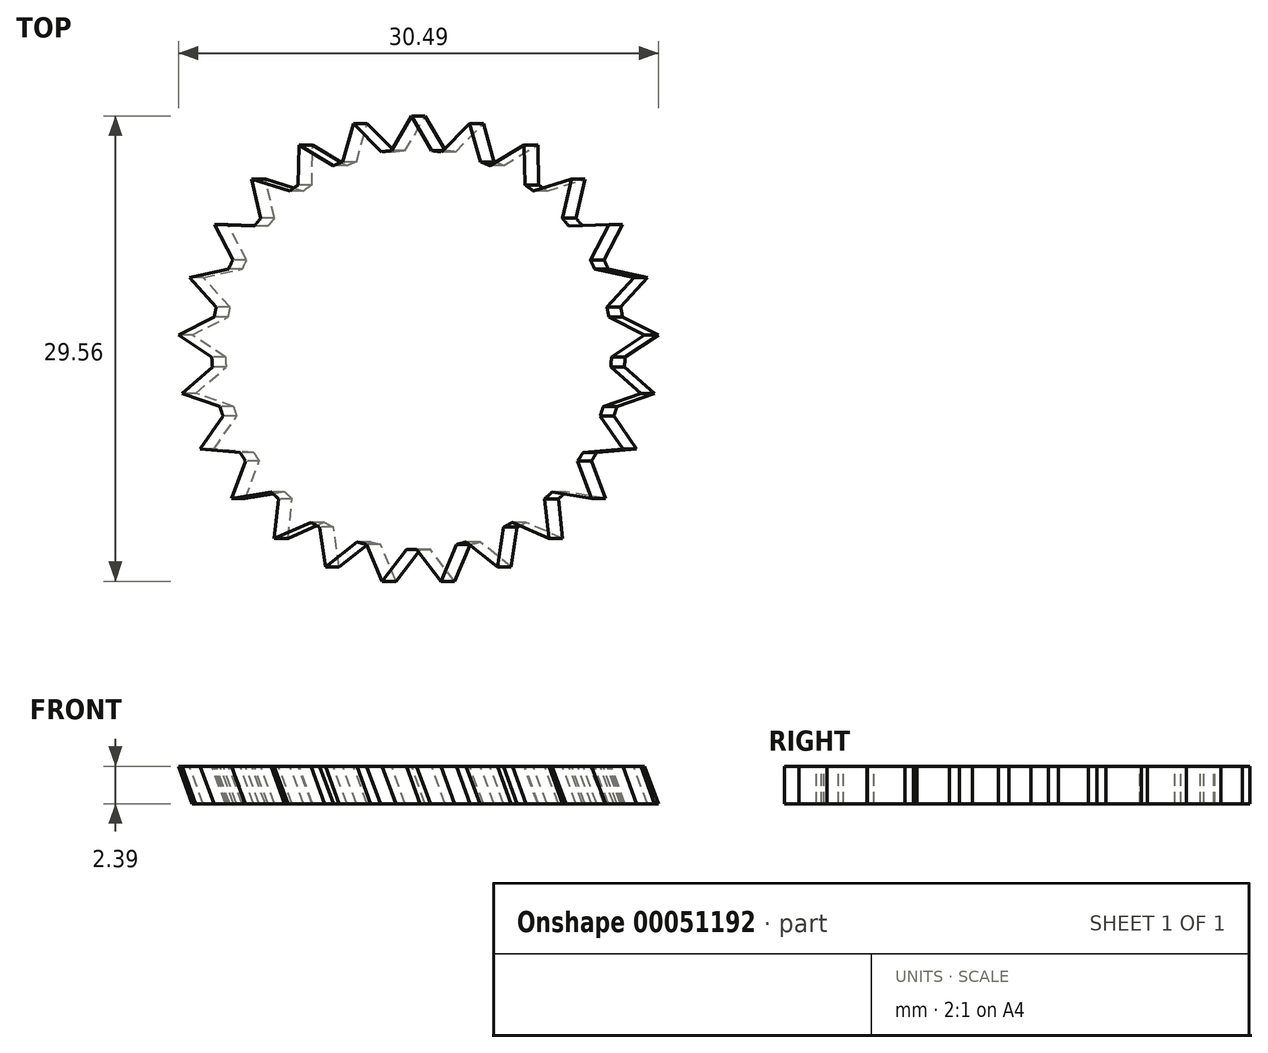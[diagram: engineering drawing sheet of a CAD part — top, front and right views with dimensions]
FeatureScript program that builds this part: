
annotation { "Feature Type Name" : "Feature", "Feature Type Description" : "" }
export const myFeature = defineFeature(function(context is Context, id is Id, definition is map)
    precondition{}
    {
        {
            var Q0;
            Q0=qCreatedBy(makeId("Top.planeOp"),FACE);
            var sketch = newSketch(context, id + "F0", { "sketchPlane" : qUnion([Q0])});
            skArc(sketch, "E0", {"start": v(-1.27, 12.64) * mm, "mid": v(-1.6, 12.6) * mm, "end": v(-1.91, 12.56) * mm});
            skLineSegment(sketch, "E1.1", {"start": v(-1.27, 12.64) * mm, "end": v(0, 14.84) * mm});
            skLineSegment(sketch, "E1.2", {"start": v(0, 14.84) * mm, "end": v(1.27, 12.64) * mm});
            skLineSegment(sketch, "E2.1.0", {"start": v(-4.37, 11.92) * mm, "end": v(-3.69, 14.37) * mm});
            skLineSegment(sketch, "E2.1.1", {"start": v(-3.69, 14.37) * mm, "end": v(-1.91, 12.56) * mm});
            skLineSegment(sketch, "E2.2.0", {"start": v(-7.2, 10.46) * mm, "end": v(-7.15, 13) * mm});
            skLineSegment(sketch, "E2.2.1", {"start": v(-7.15, 13) * mm, "end": v(-4.97, 11.69) * mm});
            skLineSegment(sketch, "E2.3.0", {"start": v(-9.58, 8.34) * mm, "end": v(-10.16, 10.82) * mm});
            skLineSegment(sketch, "E2.3.1", {"start": v(-10.16, 10.82) * mm, "end": v(-7.72, 10.08) * mm});
            skLineSegment(sketch, "E2.4.0", {"start": v(-11.35, 5.7) * mm, "end": v(-12.53, 7.95) * mm});
            skLineSegment(sketch, "E2.4.1", {"start": v(-12.53, 7.95) * mm, "end": v(-9.99, 7.84) * mm});
            skLineSegment(sketch, "E2.5.0", {"start": v(-12.41, 2.7) * mm, "end": v(-14.1, 4.58) * mm});
            skLineSegment(sketch, "E2.5.1", {"start": v(-14.1, 4.58) * mm, "end": v(-11.63, 5.11) * mm});
            skLineSegment(sketch, "E2.6.0", {"start": v(-12.7, -0.47) * mm, "end": v(-14.8, 0.93) * mm});
            skLineSegment(sketch, "E2.6.1", {"start": v(-14.8, 0.93) * mm, "end": v(-12.53, 2.06) * mm});
            skLineSegment(sketch, "E2.7.0", {"start": v(-12.17, -3.62) * mm, "end": v(-14.57, -2.78) * mm});
            skLineSegment(sketch, "E2.7.1", {"start": v(-14.57, -2.78) * mm, "end": v(-12.65, -1.12) * mm});
            skLineSegment(sketch, "E2.8.0", {"start": v(-10.9, -6.53) * mm, "end": v(-13.42, -6.32) * mm});
            skLineSegment(sketch, "E2.8.1", {"start": v(-13.42, -6.32) * mm, "end": v(-11.97, -4.23) * mm});
            skLineSegment(sketch, "E2.9.0", {"start": v(-8.93, -9.03) * mm, "end": v(-11.43, -9.46) * mm});
            skLineSegment(sketch, "E2.9.1", {"start": v(-11.43, -9.46) * mm, "end": v(-10.55, -7.08) * mm});
            skLineSegment(sketch, "E2.10.0", {"start": v(-6.4, -10.97) * mm, "end": v(-8.72, -12) * mm});
            skLineSegment(sketch, "E2.10.1", {"start": v(-8.72, -12) * mm, "end": v(-8.45, -9.48) * mm});
            skLineSegment(sketch, "E2.11.0", {"start": v(-3.47, -12.22) * mm, "end": v(-5.46, -13.8) * mm});
            skLineSegment(sketch, "E2.11.1", {"start": v(-5.46, -13.8) * mm, "end": v(-5.83, -11.28) * mm});
            skLineSegment(sketch, "E2.12.0", {"start": v(-0.32, -12.7) * mm, "end": v(-1.86, -14.72) * mm});
            skLineSegment(sketch, "E2.12.1", {"start": v(-1.86, -14.72) * mm, "end": v(-2.84, -12.38) * mm});
            skLineSegment(sketch, "E2.13.0", {"start": v(2.84, -12.38) * mm, "end": v(1.86, -14.72) * mm});
            skLineSegment(sketch, "E2.13.1", {"start": v(1.86, -14.72) * mm, "end": v(0.32, -12.7) * mm});
            skLineSegment(sketch, "E2.14.0", {"start": v(5.83, -11.28) * mm, "end": v(5.46, -13.8) * mm});
            skLineSegment(sketch, "E2.14.1", {"start": v(5.46, -13.8) * mm, "end": v(3.47, -12.22) * mm});
            skLineSegment(sketch, "E2.15.0", {"start": v(8.45, -9.48) * mm, "end": v(8.72, -12) * mm});
            skLineSegment(sketch, "E2.15.1", {"start": v(8.72, -12) * mm, "end": v(6.4, -10.97) * mm});
            skLineSegment(sketch, "E2.16.0", {"start": v(10.55, -7.08) * mm, "end": v(11.43, -9.46) * mm});
            skLineSegment(sketch, "E2.16.1", {"start": v(11.43, -9.46) * mm, "end": v(8.93, -9.03) * mm});
            skLineSegment(sketch, "E2.17.0", {"start": v(11.97, -4.23) * mm, "end": v(13.42, -6.32) * mm});
            skLineSegment(sketch, "E2.17.1", {"start": v(13.42, -6.32) * mm, "end": v(10.9, -6.53) * mm});
            skLineSegment(sketch, "E2.18.0", {"start": v(12.65, -1.12) * mm, "end": v(14.57, -2.78) * mm});
            skLineSegment(sketch, "E2.18.1", {"start": v(14.57, -2.78) * mm, "end": v(12.17, -3.62) * mm});
            skLineSegment(sketch, "E2.19.0", {"start": v(12.53, 2.06) * mm, "end": v(14.8, 0.93) * mm});
            skLineSegment(sketch, "E2.19.1", {"start": v(14.8, 0.93) * mm, "end": v(12.7, -0.47) * mm});
            skLineSegment(sketch, "E2.20.0", {"start": v(11.63, 5.11) * mm, "end": v(14.1, 4.58) * mm});
            skLineSegment(sketch, "E2.20.1", {"start": v(14.1, 4.58) * mm, "end": v(12.41, 2.7) * mm});
            skLineSegment(sketch, "E2.21.0", {"start": v(9.99, 7.84) * mm, "end": v(12.53, 7.95) * mm});
            skLineSegment(sketch, "E2.21.1", {"start": v(12.53, 7.95) * mm, "end": v(11.35, 5.7) * mm});
            skLineSegment(sketch, "E2.22.0", {"start": v(7.72, 10.08) * mm, "end": v(10.16, 10.82) * mm});
            skLineSegment(sketch, "E2.22.1", {"start": v(10.16, 10.82) * mm, "end": v(9.58, 8.34) * mm});
            skLineSegment(sketch, "E2.23.0", {"start": v(4.97, 11.69) * mm, "end": v(7.15, 13) * mm});
            skLineSegment(sketch, "E2.23.1", {"start": v(7.15, 13) * mm, "end": v(7.2, 10.46) * mm});
            skLineSegment(sketch, "E2.24.0", {"start": v(1.91, 12.56) * mm, "end": v(3.69, 14.37) * mm});
            skLineSegment(sketch, "E2.24.1", {"start": v(3.69, 14.37) * mm, "end": v(4.37, 11.92) * mm});
            skArc(sketch, "E3.trimOffspring", {"start": v(1.91, 12.56) * mm, "mid": v(1.6, 12.6) * mm, "end": v(1.27, 12.64) * mm});
            skArc(sketch, "E4.trimOffspring", {"start": v(4.97, 11.69) * mm, "mid": v(4.68, 11.8) * mm, "end": v(4.37, 11.92) * mm});
            skArc(sketch, "E5.trimOffspring", {"start": v(7.72, 10.08) * mm, "mid": v(7.46, 10.27) * mm, "end": v(7.2, 10.46) * mm});
            skArc(sketch, "E6.trimOffspring", {"start": v(9.99, 7.84) * mm, "mid": v(9.79, 8.1) * mm, "end": v(9.58, 8.34) * mm});
            skArc(sketch, "E7.trimOffspring", {"start": v(11.63, 5.11) * mm, "mid": v(11.5, 5.4) * mm, "end": v(11.35, 5.7) * mm});
            skArc(sketch, "E8.trimOffspring", {"start": v(12.53, 2.06) * mm, "mid": v(12.48, 2.38) * mm, "end": v(12.41, 2.7) * mm});
            skArc(sketch, "E9.trimOffspring", {"start": v(12.65, -1.12) * mm, "mid": v(12.67, -0.8) * mm, "end": v(12.7, -0.47) * mm});
            skArc(sketch, "E10.trimOffspring", {"start": v(11.97, -4.23) * mm, "mid": v(12.08, -3.92) * mm, "end": v(12.17, -3.62) * mm});
            skArc(sketch, "E11.trimOffspring", {"start": v(10.55, -7.08) * mm, "mid": v(10.72, -6.8) * mm, "end": v(10.9, -6.53) * mm});
            skArc(sketch, "E12.trimOffspring", {"start": v(8.45, -9.48) * mm, "mid": v(8.7, -9.26) * mm, "end": v(8.93, -9.03) * mm});
            skArc(sketch, "E13.trimOffspring", {"start": v(5.83, -11.28) * mm, "mid": v(6.12, -11.13) * mm, "end": v(6.4, -10.97) * mm});
            skArc(sketch, "E14.trimOffspring", {"start": v(2.84, -12.38) * mm, "mid": v(3.16, -12.3) * mm, "end": v(3.47, -12.22) * mm});
            skArc(sketch, "E15.trimOffspring", {"start": v(-0.32, -12.7) * mm, "mid": v(0, -12.7) * mm, "end": v(0.32, -12.7) * mm});
            skArc(sketch, "E16.trimOffspring", {"start": v(-3.47, -12.22) * mm, "mid": v(-3.16, -12.3) * mm, "end": v(-2.84, -12.38) * mm});
            skArc(sketch, "E17.trimOffspring", {"start": v(-6.4, -10.97) * mm, "mid": v(-6.12, -11.13) * mm, "end": v(-5.83, -11.28) * mm});
            skArc(sketch, "E18.trimOffspring", {"start": v(-8.93, -9.03) * mm, "mid": v(-8.7, -9.26) * mm, "end": v(-8.45, -9.48) * mm});
            skArc(sketch, "E19.trimOffspring", {"start": v(-10.9, -6.53) * mm, "mid": v(-10.72, -6.8) * mm, "end": v(-10.55, -7.08) * mm});
            skArc(sketch, "E20.trimOffspring", {"start": v(-12.17, -3.62) * mm, "mid": v(-12.08, -3.92) * mm, "end": v(-11.97, -4.23) * mm});
            skArc(sketch, "E21.trimOffspring", {"start": v(-12.7, -0.47) * mm, "mid": v(-12.67, -0.8) * mm, "end": v(-12.65, -1.12) * mm});
            skArc(sketch, "E22.trimOffspring", {"start": v(-12.41, 2.7) * mm, "mid": v(-12.48, 2.38) * mm, "end": v(-12.53, 2.06) * mm});
            skArc(sketch, "E23.trimOffspring", {"start": v(-11.35, 5.7) * mm, "mid": v(-11.5, 5.4) * mm, "end": v(-11.63, 5.11) * mm});
            skArc(sketch, "E24.trimOffspring", {"start": v(-9.58, 8.34) * mm, "mid": v(-9.79, 8.1) * mm, "end": v(-9.99, 7.84) * mm});
            skArc(sketch, "E25.trimOffspring", {"start": v(-7.2, 10.46) * mm, "mid": v(-7.46, 10.27) * mm, "end": v(-7.72, 10.08) * mm});
            skArc(sketch, "E26.trimOffspring", {"start": v(-4.37, 11.92) * mm, "mid": v(-4.68, 11.8) * mm, "end": v(-4.97, 11.69) * mm});
            skSolve(sketch);
        }
        {
            var Q0;
            Q0=qCreatedBy(makeId("Front.planeOp"),FACE);
            var sketch = newSketch(context, id + "F1", { "sketchPlane" : qUnion([Q0])});
            skLineSegment(sketch, "E27", {"start": v(0, 0) * mm, "end": v(-0.87, 2.39) * mm});
            skSolve(sketch);
        }
        {
            var Q0;
            Q0 = qSketchRegion(id + "F0", true);
            var Q1;
            Q1=sQuery(id+"F1.wireOp",EDGE,"E27");
            sweep(context, id + "F2", {"profiles" : qUnion([Q0]), "path" : qUnion([Q1])});
        }
    });
